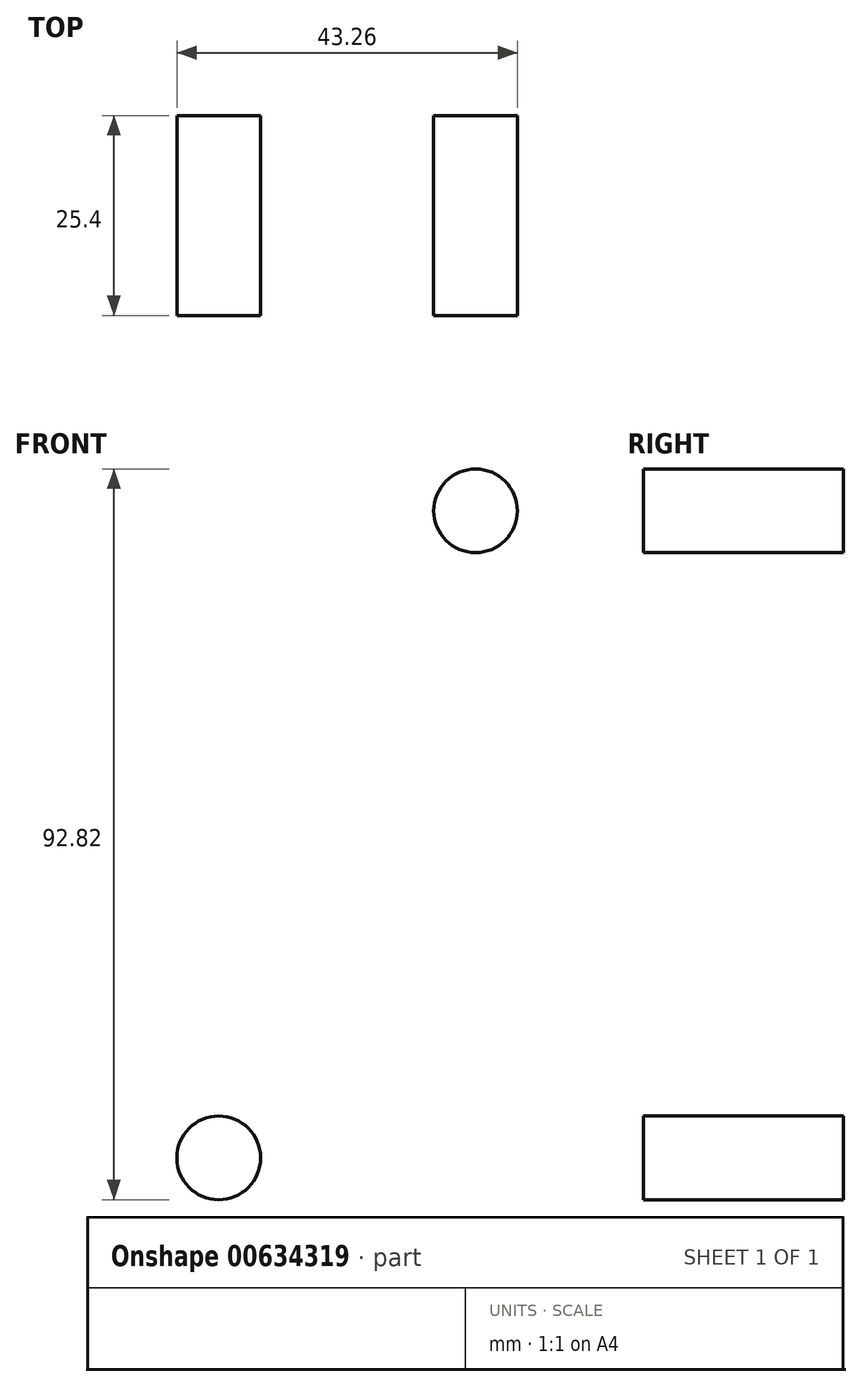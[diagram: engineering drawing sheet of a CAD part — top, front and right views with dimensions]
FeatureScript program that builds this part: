
annotation { "Feature Type Name" : "Feature", "Feature Type Description" : "" }
export const myFeature = defineFeature(function(context is Context, id is Id, definition is map)
    precondition{}
    {
        {
            var Q0;
            Q0=qCreatedBy(makeId("Front.planeOp"),FACE);
            var sketch = newSketch(context, id + "F0", { "sketchPlane" : qUnion([Q0])});
            skLineSegment(sketch, "E0.bottom", {"start": v(25.4, 50.8) * mm, "end": v(-25.4, 50.8) * mm});
            skLineSegment(sketch, "E0.top", {"start": v(25.4, -50.8) * mm, "end": v(-25.4, -50.8) * mm});
            skLineSegment(sketch, "E0.left", {"start": v(25.4, 50.8) * mm, "end": v(25.4, -50.8) * mm});
            skLineSegment(sketch, "E0.right", {"start": v(-25.4, 50.8) * mm, "end": v(-25.4, -50.8) * mm});
            skPoint(sketch, "E0.middle", {"position": v(0, 0) * mm});
            skCircle(sketch, "E1", {"center": v(0, -28.1) * mm, "radius": 7.62 * mm});
            skCircle(sketch, "E2.MirrorC", {"center": v(0, 28.1) * mm, "radius": 7.62 * mm});
            skSolve(sketch);
        }
        {
            var Q0;
            Q0 = qSketchRegion(id + "F0", true);
            extrude(context, id + "F1", {"entities" : qUnion([Q0]), "endBound" : BoundingType.SYMMETRIC, "depth" : 25.4 * mm, "offsetDistance" : 25.4 * mm});
        }
        {
            var Q0;
            Q0=makeQuery(id+"F1.opExtrude","SWEPT_EDGE",EDGE,{"disambiguationData":[OSD([sQuery(id+"F0.wireOp",EDGE,"E0.bottom"),sQuery(id+"F0.wireOp",EDGE,"E0.left")])]});
            var Q1;
            Q1=makeQuery(id+"F1.opExtrude","SWEPT_EDGE",EDGE,{"disambiguationData":[OSD([sQuery(id+"F0.wireOp",EDGE,"E0.bottom"),sQuery(id+"F0.wireOp",EDGE,"E0.right")])]});
            var Q2;
            Q2=makeQuery(id+"F1.opExtrude","SWEPT_EDGE",EDGE,{"disambiguationData":[OSD([sQuery(id+"F0.wireOp",EDGE,"E0.top"),sQuery(id+"F0.wireOp",EDGE,"E0.left")])]});
            var Q3;
            Q3=makeQuery(id+"F1.opExtrude","SWEPT_EDGE",EDGE,{"disambiguationData":[OSD([sQuery(id+"F0.wireOp",EDGE,"E0.top"),sQuery(id+"F0.wireOp",EDGE,"E0.right")])]});
            fillet(context, id + "F2", {"entities" : qUnion([Q0, Q1, Q2, Q3]), "radius" : 5.08 * mm, "tangentPropagation" : true, "allowEdgeOverflow" : false});
        }
        {
            var Q0;
            Q0=makeQuery(id+"F1.opExtrude","CAP_FACE",FACE,{"disambiguationData":[OSD([sQuery(id+"F0.wireOp",EDGE,"E0.bottom"),sQuery(id+"F0.wireOp",EDGE,"E0.top"),sQuery(id+"F0.wireOp",EDGE,"E0.left"),sQuery(id+"F0.wireOp",EDGE,"E0.right"),sQuery(id+"F0.wireOp",EDGE,"E1"),sQuery(id+"F0.wireOp",EDGE,"E2.MirrorC")])],"isStart":false});
            var sketch = newSketch(context, id + "F3", { "sketchPlane" : qUnion([Q0])});
            skCircle(sketch, "E3", {"center": v(-16.31, 41.1) * mm, "radius": 5.31 * mm});
            skCircle(sketch, "E4.MirrorC", {"center": v(16.31, 41.1) * mm, "radius": 5.31 * mm});
            skCircle(sketch, "E5.MirrorC", {"center": v(16.31, -41.1) * mm, "radius": 5.31 * mm});
            skCircle(sketch, "E6.MirrorC", {"center": v(-16.31, -41.1) * mm, "radius": 5.31 * mm});
            skSolve(sketch);
        }
        {
            var Q0;
            Q0=makeQuery(id+"F3.imprint","IMPRINT",FACE,{"disambiguationData":[TD([[makeQuery(id+"F3.imprint","IMPRINT",EDGE,{"derivedFrom":sQuery(id+"F3.wireOp",EDGE,"E3")}),1.0]])]});
            var Q1;
            Q1=makeQuery(id+"F3.imprint","IMPRINT",FACE,{"disambiguationData":[TD([[makeQuery(id+"F3.imprint","IMPRINT",EDGE,{"derivedFrom":sQuery(id+"F3.wireOp",EDGE,"E4.MirrorC")}),-1.0]])]});
            var Q2;
            Q2=makeQuery(id+"F3.imprint","IMPRINT",FACE,{"disambiguationData":[TD([[makeQuery(id+"F3.imprint","IMPRINT",EDGE,{"derivedFrom":sQuery(id+"F3.wireOp",EDGE,"E5.MirrorC")}),1.0]])]});
            var Q3;
            Q3=makeQuery(id+"F3.imprint","IMPRINT",FACE,{"disambiguationData":[TD([[makeQuery(id+"F3.imprint","IMPRINT",EDGE,{"derivedFrom":sQuery(id+"F3.wireOp",EDGE,"E6.MirrorC")}),-1.0]])]});
            var Q4;
            Q4=sQuery(id+"F3.wireOp",EDGE,"E3");
            var Q5;
            Q5=sQuery(id+"F3.wireOp",EDGE,"E4.MirrorC");
            var Q6;
            Q6=sQuery(id+"F3.wireOp",EDGE,"E5.MirrorC");
            var Q7;
            Q7=sQuery(id+"F3.wireOp",EDGE,"E6.MirrorC");
            var Q8;
            Q8=makeQuery(id+"F1.opExtrude","CAP_FACE",FACE,{"disambiguationData":[OSD([sQuery(id+"F0.wireOp",EDGE,"E0.bottom"),sQuery(id+"F0.wireOp",EDGE,"E0.top"),sQuery(id+"F0.wireOp",EDGE,"E0.left"),sQuery(id+"F0.wireOp",EDGE,"E0.right"),sQuery(id+"F0.wireOp",EDGE,"E1"),sQuery(id+"F0.wireOp",EDGE,"E2.MirrorC")])],"isStart":true});
            extrude(context, id + "F4", {"entities" : qUnion([Q0, Q1, Q2, Q3]), "operationType" : NewBodyOperationType.REMOVE, "surfaceEntities" : qUnion([Q4, Q5, Q6, Q7]), "endBound" : BoundingType.UP_TO_SURFACE, "oppositeDirection" : true, "depth" : 25.4 * mm, "endBoundEntityFace" : qUnion([Q8]), "offsetDistance" : 25.4 * mm});
        }
    });
